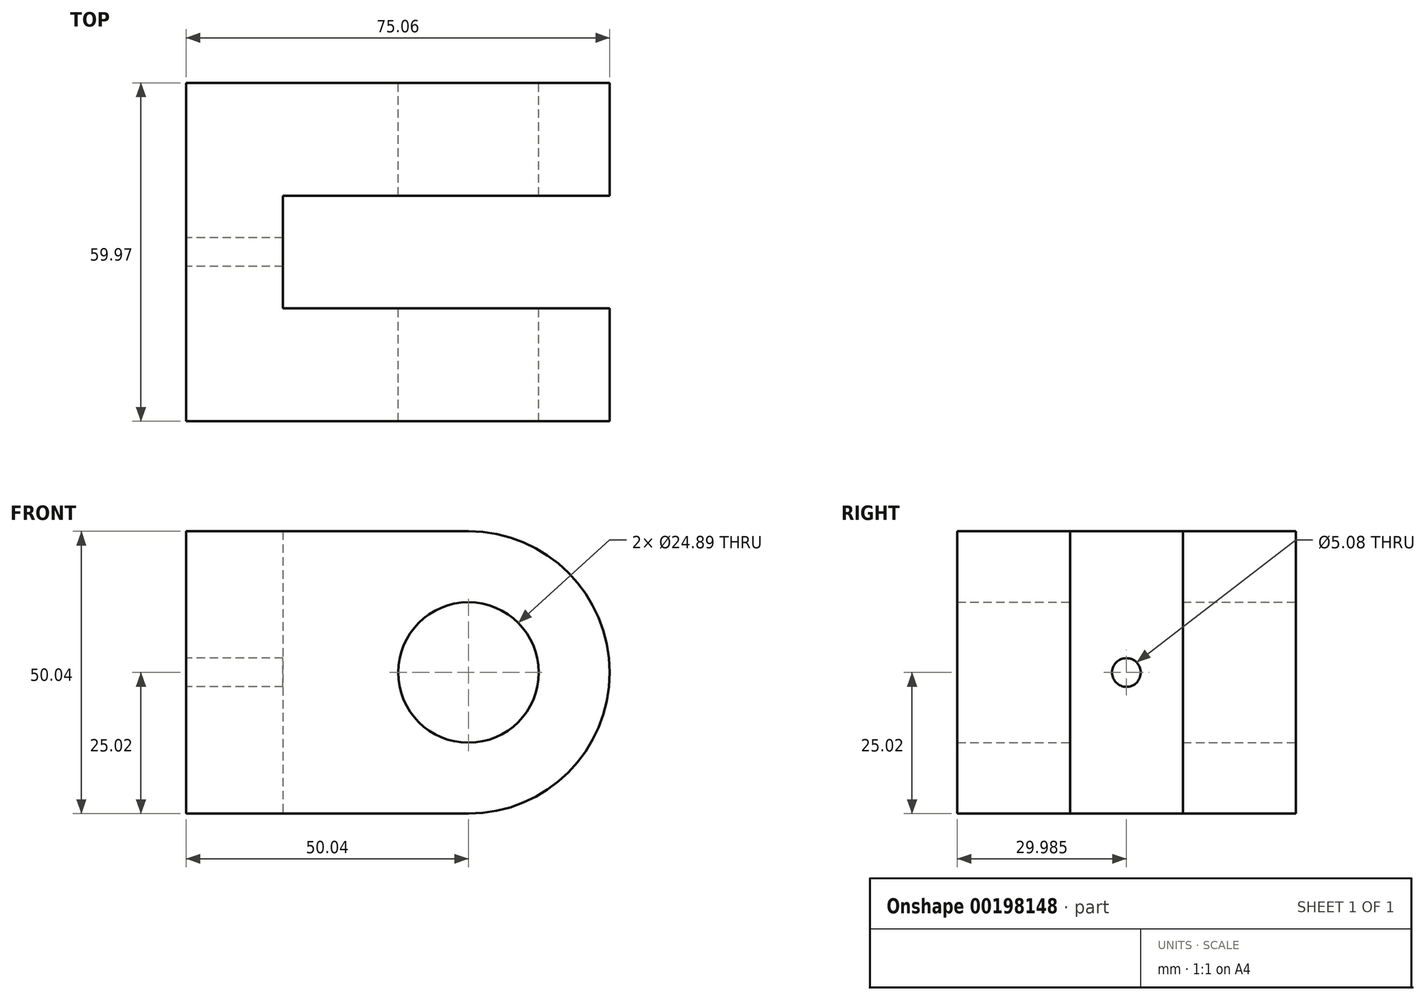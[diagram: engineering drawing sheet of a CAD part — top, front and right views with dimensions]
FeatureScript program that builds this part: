
annotation { "Feature Type Name" : "Feature", "Feature Type Description" : "" }
export const myFeature = defineFeature(function(context is Context, id is Id, definition is map)
    precondition{}
    {
        {
            var Q0;
            Q0=qCreatedBy(makeId("Front.planeOp"),FACE);
            var sketch = newSketch(context, id + "F0", { "sketchPlane" : qUnion([Q0])});
            skCircle(sketch, "E0", {"center": v(0, 0) * mm, "radius": 12.45 * mm});
            skArc(sketch, "E1", {"start": v(0, -25.02) * mm, "mid": v(25.02, 0) * mm, "end": v(0, 25.02) * mm});
            skLineSegment(sketch, "E2", {"start": v(0, 25.02) * mm, "end": v(-50.04, 25.02) * mm});
            skLineSegment(sketch, "E3", {"start": v(-50.04, 25.02) * mm, "end": v(-50.04, -25.02) * mm});
            skLineSegment(sketch, "E4", {"start": v(-50.04, -25.02) * mm, "end": v(0, -25.02) * mm});
            skSolve(sketch);
        }
        {
            var Q0;
            Q0 = qSketchRegion(id + "F0", true);
            extrude(context, id + "F1", {"entities" : qUnion([Q0]), "depth" : 19.99 * mm});
        }
        {
            var Q0;
            Q0=makeQuery(id+"F1.opExtrude","CAP_FACE",FACE,{"disambiguationData":[OSD([sQuery(id+"F0.wireOp",EDGE,"E0"),sQuery(id+"F0.wireOp",EDGE,"E1"),sQuery(id+"F0.wireOp",EDGE,"E2"),sQuery(id+"F0.wireOp",EDGE,"E3"),sQuery(id+"F0.wireOp",EDGE,"E4")])],"isStart":false});
            cPlane(context, id + "F2", {"entities" : qUnion([Q0]), "cplaneType" : CPlaneType.OFFSET, "offset" : 19.99 * mm, "width" : 152.4 * mm, "height" : 152.4 * mm});
        }
        {
            var Q0;
            Q0=qCreatedBy(id+"F2.planeOp",FACE);
            var sketch = newSketch(context, id + "F3", { "sketchPlane" : qUnion([Q0])});
            skLineSegment(sketch, "E5.0.0", {"start": v(-50.04, -25.02) * mm, "end": v(0, -25.02) * mm});
            skArc(sketch, "E5.0.1", {"start": v(0, -25.02) * mm, "mid": v(25.02, 0) * mm, "end": v(0, 25.02) * mm});
            skLineSegment(sketch, "E5.0.2", {"start": v(0, 25.02) * mm, "end": v(-50.04, 25.02) * mm});
            skLineSegment(sketch, "E5.0.3", {"start": v(-50.04, 25.02) * mm, "end": v(-50.04, -25.02) * mm});
            skCircle(sketch, "E6.0", {"center": v(0, 0) * mm, "radius": 12.45 * mm});
            skSolve(sketch);
        }
        {
            var Q0;
            Q0 = qSketchRegion(id + "F3", true);
            extrude(context, id + "F4", {"entities" : qUnion([Q0]), "depth" : 19.99 * mm});
        }
        {
            var Q0;
            Q0=makeQuery(id+"F1.opExtrude","CAP_FACE",FACE,{"disambiguationData":[OSD([sQuery(id+"F0.wireOp",EDGE,"E0"),sQuery(id+"F0.wireOp",EDGE,"E1"),sQuery(id+"F0.wireOp",EDGE,"E2"),sQuery(id+"F0.wireOp",EDGE,"E3"),sQuery(id+"F0.wireOp",EDGE,"E4")])],"isStart":false});
            var sketch = newSketch(context, id + "F5", { "sketchPlane" : qUnion([Q0])});
            skLineSegment(sketch, "E7.bottom", {"start": v(-50.04, 25.02) * mm, "end": v(-32.87, 25.02) * mm});
            skLineSegment(sketch, "E7.top", {"start": v(-50.04, -25.02) * mm, "end": v(-32.87, -25.02) * mm});
            skLineSegment(sketch, "E7.left", {"start": v(-50.04, 25.02) * mm, "end": v(-50.04, -25.02) * mm});
            skLineSegment(sketch, "E7.right", {"start": v(-32.87, 25.02) * mm, "end": v(-32.87, -25.02) * mm});
            skSolve(sketch);
        }
        {
            var Q0;
            Q0 = qSketchRegion(id + "F5", true);
            extrude(context, id + "F6", {"entities" : qUnion([Q0]), "operationType" : NewBodyOperationType.ADD, "endBound" : BoundingType.UP_TO_NEXT, "depth" : 25.4 * mm});
        }
        {
            var Q0;
            Q0=makeQuery(id+"F6.boolean.opBoolean","MERGE",FACE,{"derivedFrom":[makeQuery(id+"F1.opExtrude","SWEPT_FACE",FACE,{"disambiguationData":[OSD([sQuery(id+"F0.wireOp",EDGE,"E3")])]}),makeQuery(id+"F4.opExtrude","SWEPT_FACE",FACE,{"disambiguationData":[OSD([sQuery(id+"F3.wireOp",EDGE,"E5.0.3")])]}),makeQuery(id+"F6.opExtrude","SWEPT_FACE",FACE,{"disambiguationData":[OSD([sQuery(id+"F5.wireOp",EDGE,"E7.left")])]})]});
            var sketch = newSketch(context, id + "F7", { "sketchPlane" : qUnion([Q0])});
            skLineSegment(sketch, "E8", {"start": v(0, 0) * mm, "end": v(27.44, 0) * mm});
            skLineSegment(sketch, "E9", {"start": v(29.98, -2.54) * mm, "end": v(29.98, -25.02) * mm});
            skLineSegment(sketch, "E10", {"start": v(29.98, 2.54) * mm, "end": v(29.98, 25.02) * mm});
            skCircle(sketch, "E11", {"center": v(29.98, 0) * mm, "radius": 2.54 * mm});
            skLineSegment(sketch, "E12.trimOffspring", {"start": v(32.52, 0) * mm, "end": v(59.97, 0) * mm});
            skSolve(sketch);
        }
        {
            var Q0;
            Q0 = qSketchRegion(id + "F7", true);
            extrude(context, id + "F8", {"entities" : qUnion([Q0]), "operationType" : NewBodyOperationType.REMOVE, "endBound" : BoundingType.THROUGH_ALL, "oppositeDirection" : true, "depth" : 25.4 * mm});
        }
    });
